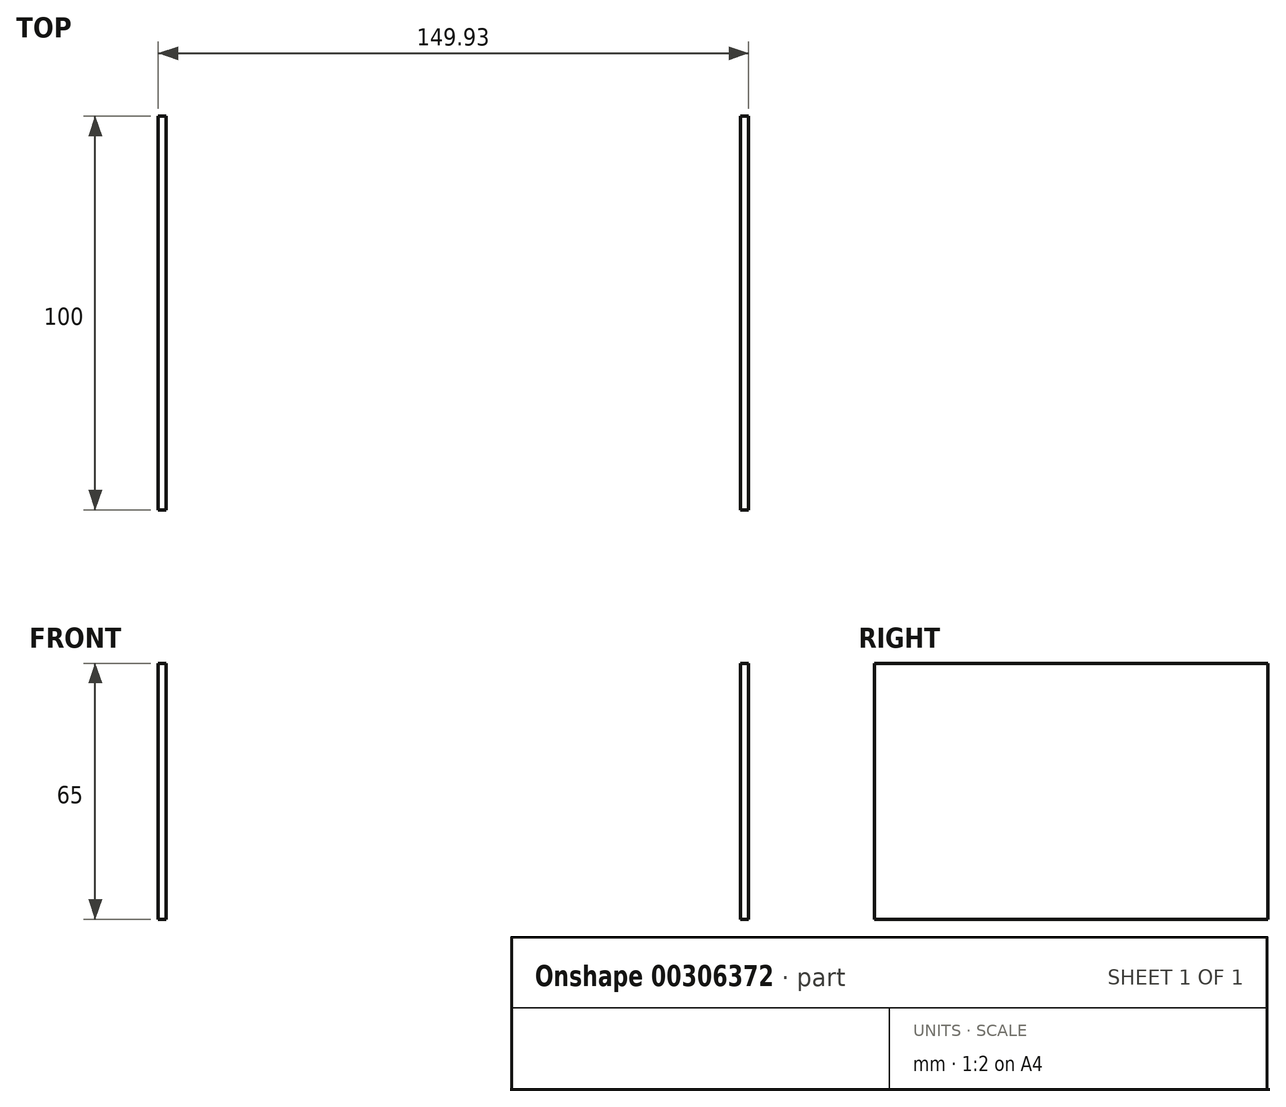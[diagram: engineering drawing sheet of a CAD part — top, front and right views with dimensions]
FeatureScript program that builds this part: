
annotation { "Feature Type Name" : "Feature", "Feature Type Description" : "" }
export const myFeature = defineFeature(function(context is Context, id is Id, definition is map)
    precondition{}
    {
        {
            var Q0;
            Q0=qCreatedBy(makeId("Front.planeOp"),FACE);
            var sketch = newSketch(context, id + "F0", { "sketchPlane" : qUnion([Q0])});
            skLineSegment(sketch, "E0.bottom", {"start": v(-75.16, 0) * mm, "end": v(-73.16, 0) * mm});
            skLineSegment(sketch, "E0.top", {"start": v(-75.16, -65) * mm, "end": v(-73.16, -65) * mm});
            skLineSegment(sketch, "E0.left", {"start": v(-75.16, 0) * mm, "end": v(-75.16, -65) * mm});
            skLineSegment(sketch, "E0.right", {"start": v(-73.16, 0) * mm, "end": v(-73.16, -65) * mm});
            skLineSegment(sketch, "E1.bottom", {"start": v(72.77, 0) * mm, "end": v(74.77, 0) * mm});
            skLineSegment(sketch, "E1.top", {"start": v(72.77, -65) * mm, "end": v(74.77, -65) * mm});
            skLineSegment(sketch, "E1.left", {"start": v(72.77, 0) * mm, "end": v(72.77, -65) * mm});
            skLineSegment(sketch, "E1.right", {"start": v(74.77, 0) * mm, "end": v(74.77, -65) * mm});
            skSolve(sketch);
        }
        {
            var Q0;
            Q0=makeQuery(id+"F0.imprint","IMPRINT",FACE,{"disambiguationData":[TD([[makeQuery(id+"F0.imprint","IMPRINT",EDGE,{"derivedFrom":sQuery(id+"F0.wireOp",EDGE,"E1.bottom")}),-1.0]])]});
            var Q1;
            Q1=makeQuery(id+"F0.imprint","IMPRINT",FACE,{"disambiguationData":[TD([[makeQuery(id+"F0.imprint","IMPRINT",EDGE,{"derivedFrom":sQuery(id+"F0.wireOp",EDGE,"E0.bottom")}),-1.0]])]});
            extrude(context, id + "F1", {"entities" : qUnion([Q0, Q1]), "depth" : 100 * mm});
        }
    });
